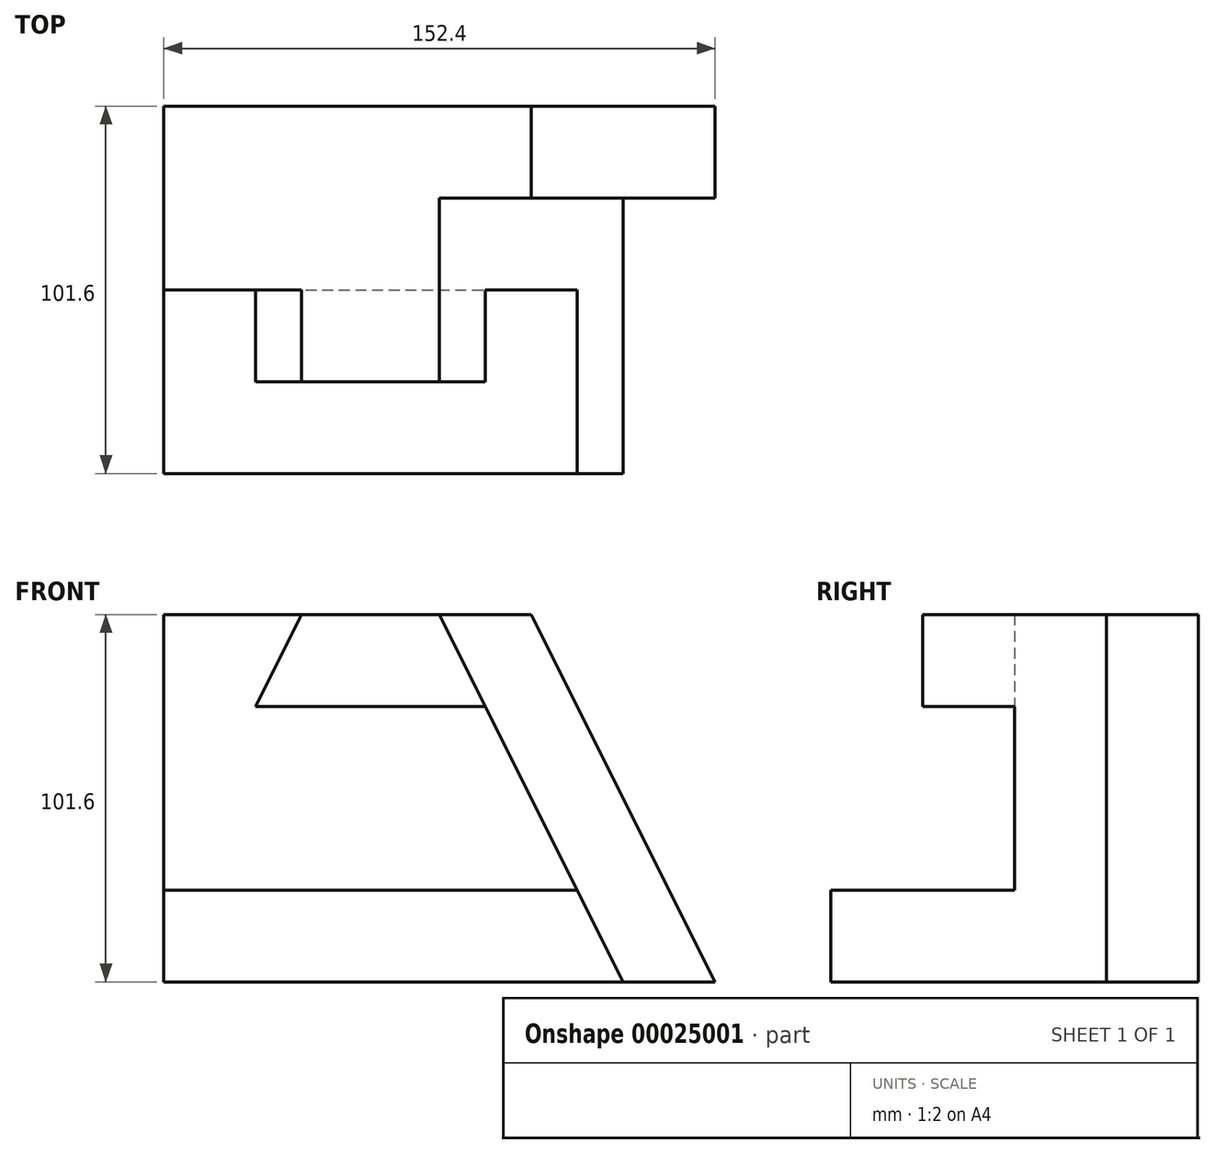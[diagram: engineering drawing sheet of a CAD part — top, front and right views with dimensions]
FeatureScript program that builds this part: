
annotation { "Feature Type Name" : "Feature", "Feature Type Description" : "" }
export const myFeature = defineFeature(function(context is Context, id is Id, definition is map)
    precondition{}
    {
        {
            var Q0;
            Q0=qCreatedBy(makeId("Front.planeOp"),FACE);
            var sketch = newSketch(context, id + "F0", { "sketchPlane" : qUnion([Q0])});
            skLineSegment(sketch, "E0.bottom", {"start": v(0, 0) * mm, "end": v(101.6, 0) * mm});
            skLineSegment(sketch, "E0.top", {"start": v(0, 101.6) * mm, "end": v(101.6, 101.6) * mm});
            skLineSegment(sketch, "E0.left", {"start": v(0, 0) * mm, "end": v(0, 101.6) * mm});
            skLineSegment(sketch, "E1", {"start": v(101.6, 101.6) * mm, "end": v(152.4, 0) * mm});
            skLineSegment(sketch, "E2", {"start": v(152.4, 0) * mm, "end": v(101.6, 0) * mm});
            skLineSegment(sketch, "E3", {"start": v(76.2, 101.6) * mm, "end": v(127, 0) * mm});
            skLineSegment(sketch, "E4", {"start": v(38.1, 101.6) * mm, "end": v(25.4, 76.2) * mm});
            skLineSegment(sketch, "E5", {"start": v(25.4, 76.2) * mm, "end": v(88.9, 76.2) * mm});
            skLineSegment(sketch, "E6", {"start": v(0, 25.4) * mm, "end": v(114.3, 25.4) * mm});
            skSolve(sketch);
        }
        {
            var Q0;
            {var subQ7=sQuery(id+"F0.wireOp",EDGE,"E1");Q0=makeQuery(id+"F0.imprint","IMPRINT",FACE,{"disambiguationData":[TD([[makeQuery(id+"F0.imprint","IMPRINT",EDGE,{"derivedFrom":subQ7}),-1.0]])]});}
            extrude(context, id + "F1", {"entities" : qUnion([Q0]), "depth" : 25.4 * mm});
        }
        {
            var Q0;
            {var subQ2=sQuery(id+"F0.wireOp",EDGE,"E4");Q0=makeQuery(id+"F0.imprint","IMPRINT",FACE,{"disambiguationData":[TD([[makeQuery(id+"F0.imprint","IMPRINT",EDGE,{"derivedFrom":subQ2}),-1.0]])]});}
            extrude(context, id + "F2", {"entities" : qUnion([Q0]), "operationType" : NewBodyOperationType.ADD, "depth" : 50.8 * mm});
        }
        {
            var Q0;
            {var subQ1=sQuery(id+"F0.wireOp",EDGE,"E4");Q0=makeQuery(id+"F0.imprint","IMPRINT",FACE,{"disambiguationData":[TD([[makeQuery(id+"F0.imprint","IMPRINT",EDGE,{"derivedFrom":subQ1}),1.0]])]});}
            extrude(context, id + "F3", {"entities" : qUnion([Q0]), "operationType" : NewBodyOperationType.ADD, "depth" : 76.2 * mm});
        }
        {
            var Q0;
            {var subQ4=sQuery(id+"F0.wireOp",EDGE,"E0.bottom");Q0=makeQuery(id+"F0.imprint","IMPRINT",FACE,{"disambiguationData":[TD([[makeQuery(id+"F0.imprint","IMPRINT",EDGE,{"derivedFrom":subQ4}),1.0]])]});}
            extrude(context, id + "F4", {"entities" : qUnion([Q0]), "operationType" : NewBodyOperationType.ADD, "depth" : 101.6 * mm});
        }
    });
